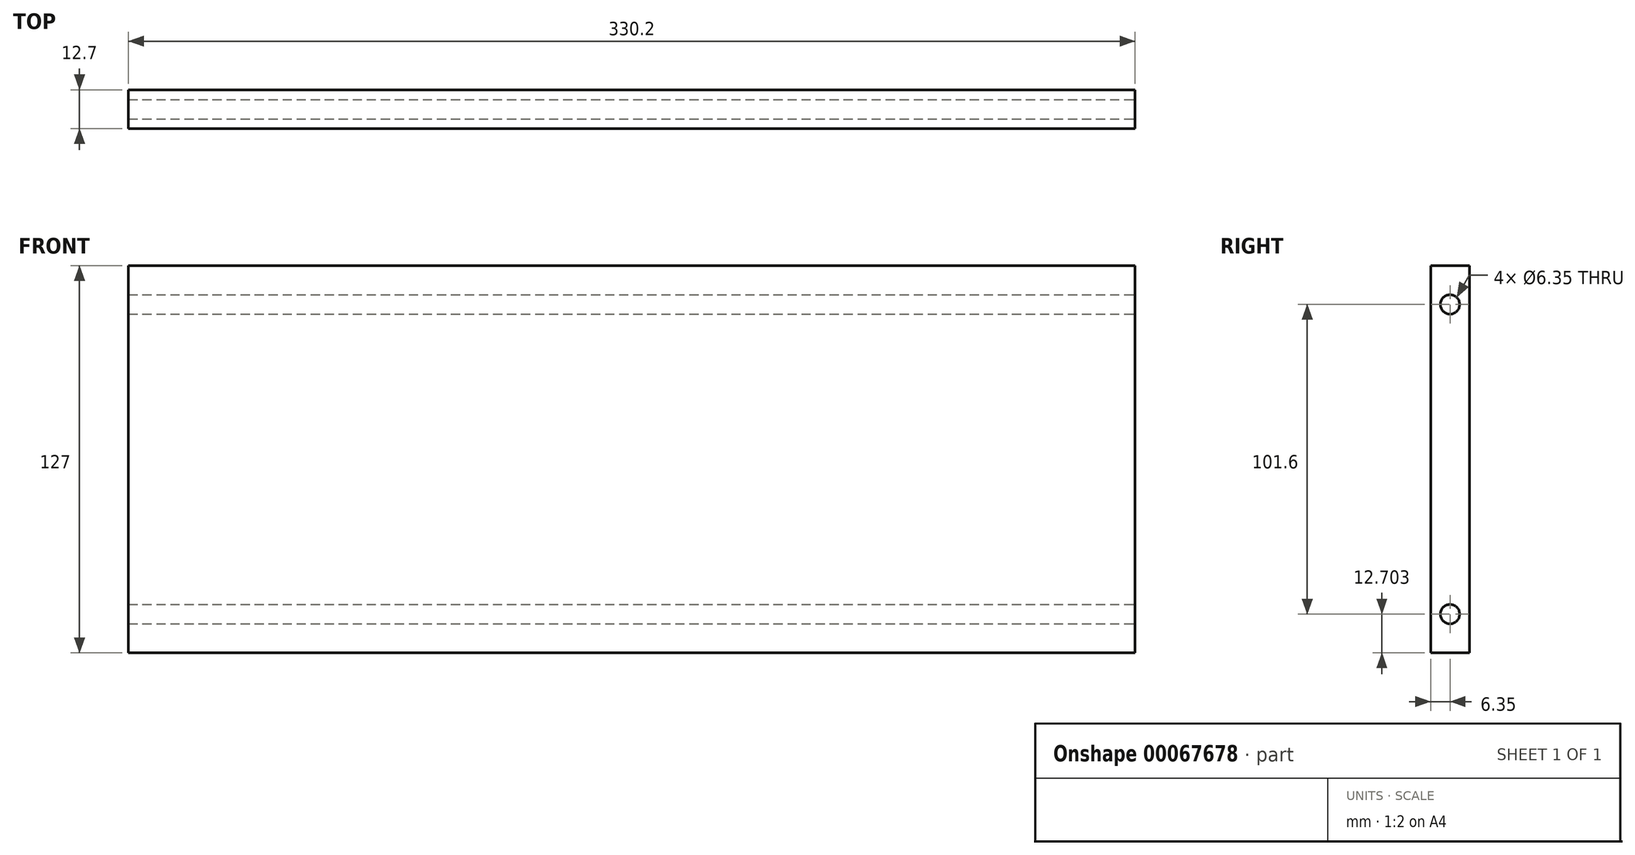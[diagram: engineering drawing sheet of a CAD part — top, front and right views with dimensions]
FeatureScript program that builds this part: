
annotation { "Feature Type Name" : "Feature", "Feature Type Description" : "" }
export const myFeature = defineFeature(function(context is Context, id is Id, definition is map)
    precondition{}
    {
        {
            var Q0;
            Q0=qCreatedBy(makeId("Front.planeOp"),FACE);
            var sketch = newSketch(context, id + "F0", { "sketchPlane" : qUnion([Q0])});
            skLineSegment(sketch, "E0.bottom", {"start": v(-110.65, 65.73) * mm, "end": v(219.55, 65.73) * mm});
            skLineSegment(sketch, "E0.top", {"start": v(-110.65, -61.27) * mm, "end": v(219.55, -61.27) * mm});
            skLineSegment(sketch, "E0.left", {"start": v(-110.65, 65.73) * mm, "end": v(-110.65, -61.27) * mm});
            skLineSegment(sketch, "E0.right", {"start": v(219.55, 65.73) * mm, "end": v(219.55, -61.27) * mm});
            skSolve(sketch);
        }
        {
            var Q0;
            Q0=makeQuery(id+"F0.imprint","IMPRINT",FACE,{"disambiguationData":[TD([[makeQuery(id+"F0.imprint","IMPRINT",EDGE,{"derivedFrom":sQuery(id+"F0.wireOp",EDGE,"E0.bottom")}),-1.0]])]});
            extrude(context, id + "F1", {"entities" : qUnion([Q0]), "depth" : 12.7 * mm});
        }
        {
            var Q0;
            Q0=makeQuery(id+"F1.opExtrude","SWEPT_FACE",FACE,{"disambiguationData":[OSD([sQuery(id+"F0.wireOp",EDGE,"E0.right")])]});
            var sketch = newSketch(context, id + "F2", { "sketchPlane" : qUnion([Q0])});
            skPoint(sketch, "E1", {"position": v(-6.35, 53.03) * mm});
            skPoint(sketch, "E2", {"position": v(-6.35, -48.57) * mm});
            skSolve(sketch);
        }
        {
            var Q0;
            Q0=sQuery(id+"F2.wireOp",VERTEX,"E1");
            var Q1;
            Q1=sQuery(id+"F2.wireOp",VERTEX,"E2");
            var Q2;
            Q2=makeQuery(id+"F1.opExtrude","SWEPT_BODY",BODY,{"disambiguationData":[OSD([sQuery(id+"F0.wireOp",EDGE,"E0.bottom"),sQuery(id+"F0.wireOp",EDGE,"E0.top"),sQuery(id+"F0.wireOp",EDGE,"E0.left"),sQuery(id+"F0.wireOp",EDGE,"E0.right")])]});
            hole(context, id + "F3", {"style" : HoleStyle.SIMPLE, "holeDiameter" : 6.35 * mm, "endStyle" : HoleEndStyle.THROUGH, "locations" : qUnion([Q0, Q1]), "scope" : qUnion([Q2])});
        }
    });
